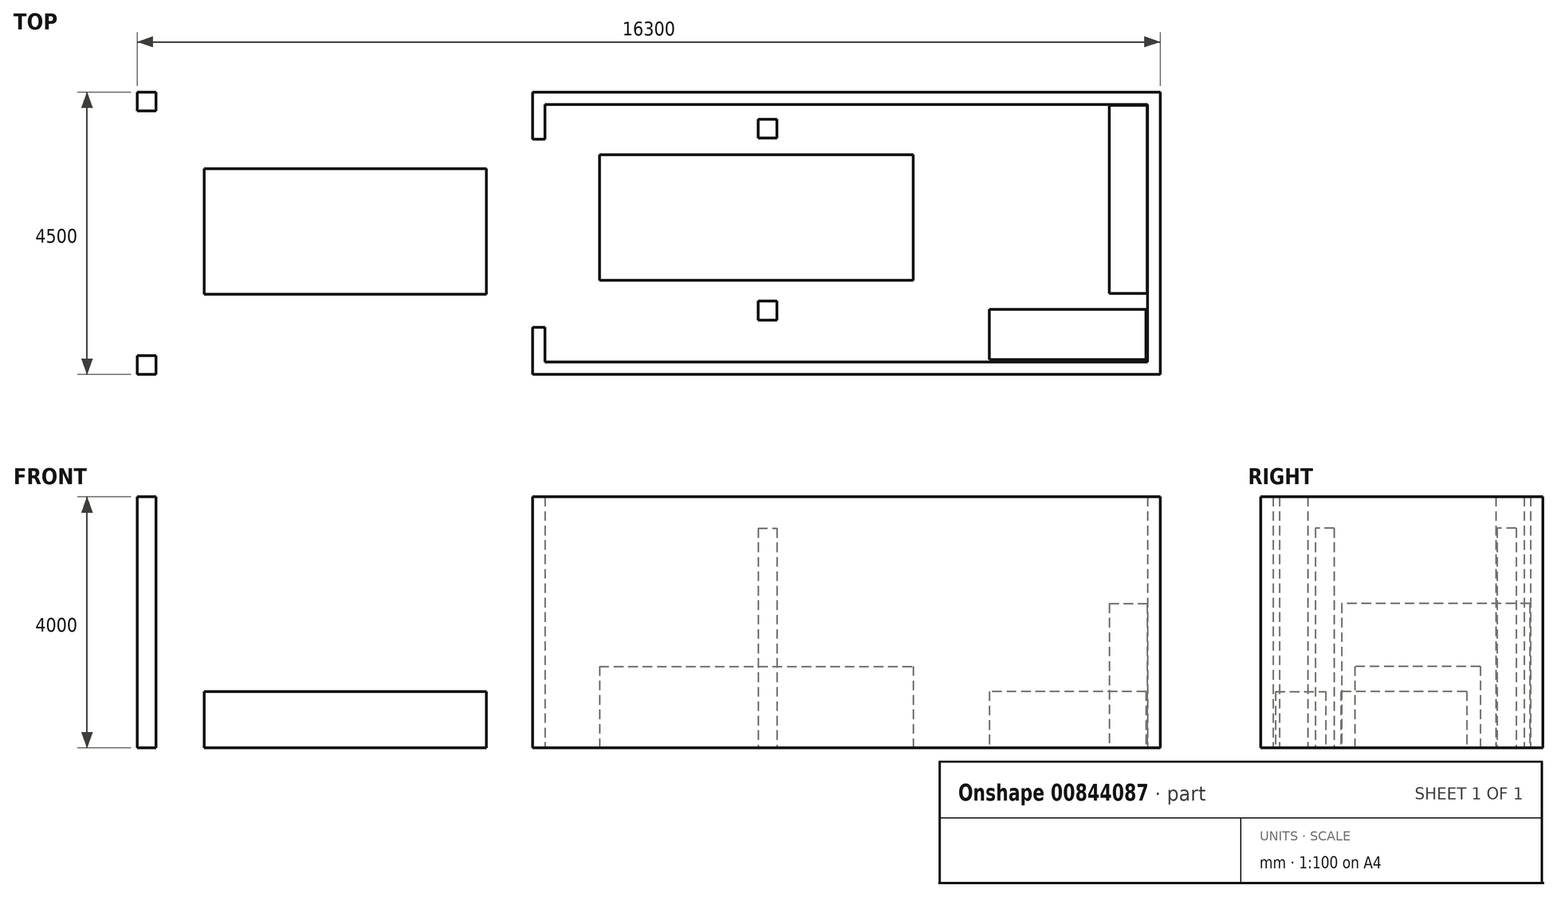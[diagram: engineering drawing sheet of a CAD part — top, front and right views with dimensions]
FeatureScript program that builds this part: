
annotation { "Feature Type Name" : "Feature", "Feature Type Description" : "" }
export const myFeature = defineFeature(function(context is Context, id is Id, definition is map)
    precondition{}
    {
        {
            var Q0;
            Q0=qCreatedBy(makeId("Top.planeOp"),FACE);
            var sketch = newSketch(context, id + "F0", { "sketchPlane" : qUnion([Q0])});
            skLineSegment(sketch, "E0.bottom", {"start": v(0, 0) * mm, "end": v(10000, 0) * mm});
            skLineSegment(sketch, "E0.top", {"start": v(0, 4500) * mm, "end": v(10000, 4500) * mm});
            skLineSegment(sketch, "E0.left", {"start": v(0, 0) * mm, "end": v(0, 750) * mm});
            skLineSegment(sketch, "E0.right", {"start": v(10000, 0) * mm, "end": v(10000, 4500) * mm});
            skLineSegment(sketch, "E1", {"start": v(-2641.31, 2250) * mm, "end": v(18016.81, 2250) * mm, "construction": true});
            skLineSegment(sketch, "E2.bottom", {"start": v(200, 4300) * mm, "end": v(9800, 4300) * mm});
            skLineSegment(sketch, "E2.top", {"start": v(200, 200) * mm, "end": v(9800, 200) * mm});
            skLineSegment(sketch, "E2.left", {"start": v(200, 4300) * mm, "end": v(200, 3750) * mm});
            skLineSegment(sketch, "E2.right", {"start": v(9800, 4300) * mm, "end": v(9800, 200) * mm});
            skLineSegment(sketch, "E3", {"start": v(0, 3750) * mm, "end": v(200, 3750) * mm});
            skLineSegment(sketch, "E4", {"start": v(0, 750) * mm, "end": v(200, 750) * mm});
            skLineSegment(sketch, "E5.trimOffspring", {"start": v(200, 750) * mm, "end": v(200, 200) * mm});
            skLineSegment(sketch, "E6.trimOffspring", {"start": v(0, 3750) * mm, "end": v(0, 4500) * mm});
            skLineSegment(sketch, "E7", {"start": v(0, 4500) * mm, "end": v(-12401.9, 4500) * mm, "construction": true});
            skLineSegment(sketch, "E8", {"start": v(-12401.9, 4500) * mm, "end": v(-12401.9, 0) * mm, "construction": true});
            skLineSegment(sketch, "E9.bottom", {"start": v(-6300, 4500) * mm, "end": v(-6000, 4500) * mm});
            skLineSegment(sketch, "E9.top", {"start": v(-6300, 4200) * mm, "end": v(-6000, 4200) * mm});
            skLineSegment(sketch, "E9.left", {"start": v(-6300, 4500) * mm, "end": v(-6300, 4200) * mm});
            skLineSegment(sketch, "E9.right", {"start": v(-6000, 4500) * mm, "end": v(-6000, 4200) * mm});
            skLineSegment(sketch, "E10.bottom", {"start": v(-6300, 0) * mm, "end": v(-6000, 0) * mm});
            skLineSegment(sketch, "E10.top", {"start": v(-6300, 300) * mm, "end": v(-6000, 300) * mm});
            skLineSegment(sketch, "E10.left", {"start": v(-6300, 0) * mm, "end": v(-6300, 300) * mm});
            skLineSegment(sketch, "E10.right", {"start": v(-6000, 0) * mm, "end": v(-6000, 300) * mm});
            skLineSegment(sketch, "E11", {"start": v(-12401.9, 0) * mm, "end": v(0, 0) * mm, "construction": true});
            skSolve(sketch);
        }
        {
            var Q0;
            Q0=makeQuery(id+"F0.imprint","IMPRINT",FACE,{"disambiguationData":[TD([[makeQuery(id+"F0.imprint","IMPRINT",EDGE,{"derivedFrom":sQuery(id+"F0.wireOp",EDGE,"E0.bottom")}),1.0]])]});
            var Q1;
            Q1=makeQuery(id+"F0.imprint","IMPRINT",FACE,{"disambiguationData":[TD([[makeQuery(id+"F0.imprint","IMPRINT",EDGE,{"derivedFrom":sQuery(id+"F0.wireOp",EDGE,"E9.bottom")}),-1.0]])]});
            var Q2;
            Q2=makeQuery(id+"F0.imprint","IMPRINT",FACE,{"disambiguationData":[TD([[makeQuery(id+"F0.imprint","IMPRINT",EDGE,{"derivedFrom":sQuery(id+"F0.wireOp",EDGE,"E10.bottom")}),1.0]])]});
            extrude(context, id + "F1", {"entities" : qUnion([Q0, Q1, Q2]), "depth" : 4000 * mm, "offsetDistance" : 25 * mm});
        }
        {
            var Q0;
            Q0=qCreatedBy(makeId("Top.planeOp"),FACE);
            var sketch = newSketch(context, id + "F2", { "sketchPlane" : qUnion([Q0])});
            skLineSegment(sketch, "E12.bottom", {"start": v(1065.62, 3500) * mm, "end": v(6065.62, 3500) * mm});
            skLineSegment(sketch, "E12.top", {"start": v(1065.62, 1500) * mm, "end": v(6065.62, 1500) * mm});
            skLineSegment(sketch, "E12.left", {"start": v(1065.62, 3500) * mm, "end": v(1065.62, 1500) * mm});
            skLineSegment(sketch, "E12.right", {"start": v(6065.62, 3500) * mm, "end": v(6065.62, 1500) * mm});
            skLineSegment(sketch, "E13.bottom", {"start": v(-5233.64, 3281.4) * mm, "end": v(-733.64, 3281.4) * mm});
            skLineSegment(sketch, "E13.top", {"start": v(-5233.64, 1281.4) * mm, "end": v(-733.64, 1281.4) * mm});
            skLineSegment(sketch, "E13.left", {"start": v(-5233.64, 3281.4) * mm, "end": v(-5233.64, 1281.4) * mm});
            skLineSegment(sketch, "E13.right", {"start": v(-733.64, 3281.4) * mm, "end": v(-733.64, 1281.4) * mm});
            skSolve(sketch);
        }
        {
            var Q0;
            Q0=makeQuery(id+"F2.imprint","IMPRINT",FACE,{"disambiguationData":[TD([[makeQuery(id+"F2.imprint","IMPRINT",EDGE,{"derivedFrom":sQuery(id+"F2.wireOp",EDGE,"E12.bottom")}),-1.0]])]});
            extrude(context, id + "F3", {"entities" : qUnion([Q0]), "depth" : 1300 * mm, "offsetDistance" : 25 * mm});
        }
        {
            var Q0;
            Q0=qCreatedBy(makeId("Top.planeOp"),FACE);
            var sketch = newSketch(context, id + "F4", { "sketchPlane" : qUnion([Q0])});
            skLineSegment(sketch, "E14.bottom", {"start": v(9188.86, 4289.35) * mm, "end": v(9788.86, 4289.35) * mm});
            skLineSegment(sketch, "E14.top", {"start": v(9188.86, 1289.35) * mm, "end": v(9788.86, 1289.35) * mm});
            skLineSegment(sketch, "E14.left", {"start": v(9188.86, 4289.35) * mm, "end": v(9188.86, 1289.35) * mm});
            skLineSegment(sketch, "E14.right", {"start": v(9788.86, 4289.35) * mm, "end": v(9788.86, 1289.35) * mm});
            skLineSegment(sketch, "E15.bottom", {"start": v(9774.82, 235.98) * mm, "end": v(7274.82, 235.98) * mm});
            skLineSegment(sketch, "E15.top", {"start": v(9774.82, 1035.98) * mm, "end": v(7274.82, 1035.98) * mm});
            skLineSegment(sketch, "E15.left", {"start": v(9774.82, 235.98) * mm, "end": v(9774.82, 1035.98) * mm});
            skLineSegment(sketch, "E15.right", {"start": v(7274.82, 235.98) * mm, "end": v(7274.82, 1035.98) * mm});
            skSolve(sketch);
        }
        {
            var Q0;
            Q0=makeQuery(id+"F4.imprint","IMPRINT",FACE,{"disambiguationData":[TD([[makeQuery(id+"F4.imprint","IMPRINT",EDGE,{"derivedFrom":sQuery(id+"F4.wireOp",EDGE,"E14.bottom")}),-1.0]])]});
            extrude(context, id + "F5", {"entities" : qUnion([Q0]), "depth" : 2300 * mm, "offsetDistance" : 25 * mm});
        }
        {
            var Q0;
            Q0=makeQuery(id+"F2.imprint","IMPRINT",FACE,{"disambiguationData":[TD([[makeQuery(id+"F2.imprint","IMPRINT",EDGE,{"derivedFrom":sQuery(id+"F2.wireOp",EDGE,"E13.bottom")}),-1.0]])]});
            extrude(context, id + "F6", {"entities" : qUnion([Q0]), "depth" : 900 * mm, "offsetDistance" : 25 * mm});
        }
        {
            var Q0;
            Q0=qCreatedBy(makeId("Top.planeOp"),FACE);
            var sketch = newSketch(context, id + "F7", { "sketchPlane" : qUnion([Q0])});
            skLineSegment(sketch, "E16.bottom", {"start": v(3592.67, 4068.8) * mm, "end": v(3892.67, 4068.8) * mm});
            skLineSegment(sketch, "E16.top", {"start": v(3592.67, 3768.8) * mm, "end": v(3892.67, 3768.8) * mm});
            skLineSegment(sketch, "E16.left", {"start": v(3592.67, 4068.8) * mm, "end": v(3592.67, 3768.8) * mm});
            skLineSegment(sketch, "E16.right", {"start": v(3892.67, 4068.8) * mm, "end": v(3892.67, 3768.8) * mm});
            skLineSegment(sketch, "E17", {"start": v(3592.67, 3768.8) * mm, "end": v(3592.67, 1168.8) * mm, "construction": true});
            skLineSegment(sketch, "E18.bottom", {"start": v(3592.67, 1168.8) * mm, "end": v(3892.67, 1168.8) * mm});
            skLineSegment(sketch, "E18.top", {"start": v(3592.67, 868.8) * mm, "end": v(3892.67, 868.8) * mm});
            skLineSegment(sketch, "E18.left", {"start": v(3592.67, 1168.8) * mm, "end": v(3592.67, 868.8) * mm});
            skLineSegment(sketch, "E18.right", {"start": v(3892.67, 1168.8) * mm, "end": v(3892.67, 868.8) * mm});
            skSolve(sketch);
        }
        {
            var Q0;
            Q0=makeQuery(id+"F7.imprint","IMPRINT",FACE,{"disambiguationData":[TD([[makeQuery(id+"F7.imprint","IMPRINT",EDGE,{"derivedFrom":sQuery(id+"F7.wireOp",EDGE,"E16.bottom")}),-1.0]])]});
            var Q1;
            Q1=makeQuery(id+"F7.imprint","IMPRINT",FACE,{"disambiguationData":[TD([[makeQuery(id+"F7.imprint","IMPRINT",EDGE,{"derivedFrom":sQuery(id+"F7.wireOp",EDGE,"E18.bottom")}),-1.0]])]});
            extrude(context, id + "F8", {"entities" : qUnion([Q0, Q1]), "depth" : 3500 * mm, "offsetDistance" : 25 * mm});
        }
        {
            var Q0;
            Q0=makeQuery(id+"F4.imprint","IMPRINT",FACE,{"disambiguationData":[TD([[makeQuery(id+"F4.imprint","IMPRINT",EDGE,{"derivedFrom":sQuery(id+"F4.wireOp",EDGE,"E15.bottom")}),-1.0]])]});
            extrude(context, id + "F9", {"entities" : qUnion([Q0]), "depth" : 900 * mm, "offsetDistance" : 25 * mm});
        }
    });
